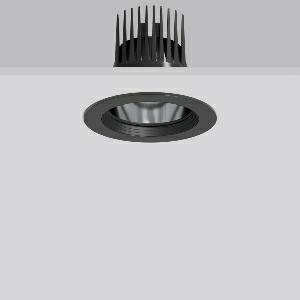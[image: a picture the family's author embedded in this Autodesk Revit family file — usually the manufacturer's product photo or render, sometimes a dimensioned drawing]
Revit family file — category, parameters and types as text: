
# Revit family: heledon_maxi_e_901756_003_2_76_0338
name_source: partatom
category: Lighting Fixtures
units: mm (PartAtom-declared; Revit-internal decimal feet)

## family parameters
Cut with Voids When Loaded = No
Host = Face
Light Source = No
Part Type = Normal
Room Calculation Point = No
Round Connector Dimension = Use Diameter
Shared = No

## types (1)
- HELEDON maxi E (1 x LED Modul 927, 3050 lm, 2700)
    Apparent Load = 25 VA
    Approval mark = CE
    CIE Flux Codes = 100 100 100 100 100
    Color Rendering = 92
    Color Temperature = 2700
    Default Elevation = 1800 mm
    Description = Series: HELEDON maxi
Round recessed downlight. Housing: die-cast aluminium, powder-coated. Black plastic ring and recessed LED to prevent glare from the side. Optical assembly with reflector made of MIRO-Silver with 98% total light reflection for outstanding efficiency - can be changed without tools. Best colour rendering index Ra>90. Suitable for Recessed ceiling mounting. Installation without tools thanks to spring fastening system. Including separate LED converter with connecting cable 600 mm.High quality converter without flickering and stroboscopic effect. Through-wiring box (5 pole) available as accessory. The following accessories can be mounted without use of tools: interchangeable lenses, decorative glasses, honeycomb louvre, clear and frosted diffusers, white interchangeable plastic ring. 
Colour: deep black, matt (RAL 9005)
Diameter: 162 mm
Height: 3 mm
Cut-out diameter: 152 mm
Recess height: 200 mm
Luminaire: recess height: 135 mm
Lamp: LED
Socket: without socket
Colour temperature: 2700K
Colour rendering index (CRI): 92
System power: 25 W
Rated luminous flux: 3050 lm
Luminous efficiency: 122 lm/W
Control gear: Converter, dimmable, DALI
Protection class: II
Type of protection: IP 20
    Height = 0 mm  [stored 0 ft]
    Lamp = 1 x LED Modul 927
    Lamp Light Flux = 3050 lm
    Lamp count = 1
    Length = 162 mm
    Lifetime = 50000 h
    Luminous efficacy = 122 lm/W
    Manufacturer = RZB
    ModVariant = No
    Model = 901756.003.2.76
    Mounting Place = Ceiling
    Mounting Type = Recessed
    Number of Poles = 1
    OnlyDefault = Yes
    Power Factor = 1
    Product Name = HELEDON maxi E
    Product group = Recessed downlights
    ProductGroupID = 402
    Protection Class = Protection class II
    Protection Degree = IP 20
    RLX_Detail_Level = 1
    RLX_Emergency_Light_Flux = 0 lm
    RLX_Emergency_Type = 0
    RLX_Emergency_Type_DB = No
    RlxData = <blob elided: 123549 chars, md5=ebc98bff>
    Socket = socket
    Standby Power = 0 W
    System Light Flux = 3050 lm
    System Power = 25 W
    Type Comments = Product without accessories
    Type Image = 901662.003.jpg
    URL = http://relux.com
    VarID = ---
    Voltage = 230 V
    Voltage Range = 220-240 V
    Weight = 0.00 kg
    Width = 0 mm  [stored 0 ft]

note: [stored X ft] marks values corroborated as IEEE doubles in the binary element streams (Revit-internal decimal feet)

## geometry (parser evidence)
native form markers: Blend x4, Sweep x11
no freeform markers — native parametric forms only
